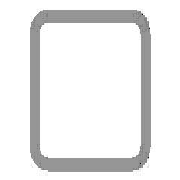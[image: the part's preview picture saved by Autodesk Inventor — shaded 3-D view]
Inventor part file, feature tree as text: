
AUTODESK INVENTOR PART (.ipt)
format: ipt  version: 2024 (Build 280153000, 153)  size: 128,512 bytes
history: native  units: mm (DEFAULTED — no unit token found)
features: other x4, extrude x1, sketch x1, plane x1
ambient origin geometry x8: Origin, YZ Plane, XZ Plane, XY Plane, X Axis, Y Axis, Z Axis, Center Point
bodies: Solid1 (feature_tree)
feature tree (7):
  parser-record x1  (decoder bookkeeping rows leaked as tree rows — omitted from the tree; the rows remain in map.json)
  other  "Driven Length"
  other  "Plano inicial"
  other  "Plano final"
  extrude  "Cuerpo"  TaperAngle=0.0deg  [1 undecoded]
  sketch  "Sketch3"  dims[d3=2090.0mm d4=0.0mm d10=50.8mm d11=50.8mm d12=3.175mm d13=-0.0mm d14=2090.0mm d15=25.4mm d16=25.4mm d17=6.35mm d18=90.0deg d19=2090.0mm]
  plane  "Work Plane3"
note: 1 required parameter value undecoded (feature->parameter linkage not recoverable at this tier; creation-order binding heuristic only, values carry confidence <= 0.55)
